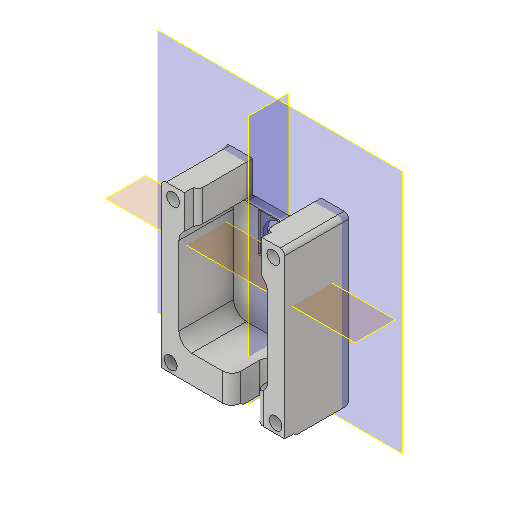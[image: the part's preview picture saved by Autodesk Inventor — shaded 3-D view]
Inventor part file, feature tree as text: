
AUTODESK INVENTOR PART (.ipt)
format: ipt  version: 2022 (Build 260153000, 153)  size: 474,624 bytes
history: native  units: mm
features: reference x19, other x12, sketch x11, extrude x10, projected_geometry x8, plane x5, fillet x2, hole x2, chamfer x1
ambient origin geometry x8: Origin, YZ Plane, XZ Plane, XY Plane, X Axis, Y Axis, Z Axis, Center Point
bodies: Solid1 (feature_tree)
feature tree (70):
  plane  "Work Plane1"
  extrude  "Extrusion1"  Depth=53.8mm
  extrude  "IM_offset"  Depth=53.8mm
  plane  "Arbeitsebene5"
  plane  "Arbeitsebene6"
  extrude  "Extrusion26"  Depth=45.0mm
  chamfer  "Fase2"  Distance=0.1mm
  plane  "Arbeitsebene9"
  extrude  "Extrusion29"  Depth=10.0mm
  extrude  "Extrusion30"  Depth=10.0mm
  plane  "Arbeitsebene10"
  extrude  "Extrusion31"  Depth=10.0mm TaperAngle=0.0deg
  fillet  "Rundung3"  Radius=7.5mm
  hole  "Bohrung2"  [1 undecoded]
  extrude  "Extrusion32"  Depth=2.0mm TaperAngle=45.0deg
  hole  "Bohrung3"  [1 undecoded]
  extrude  "Extrusion33"  Depth=10.0mm
  extrude  "Extrusion34"  Depth=10.0mm
  fillet  "Rundung4"  [1 undecoded]
  extrude  "Extrusion35"  Depth=10.0mm TaperAngle=0.0deg
  sketch  "Sketch1"  dims[d10=12.0mm d11=0.0mm d18=53.8mm]
  reference  "Reference1"
  reference  "Reference2"
  reference  "Reference3"
  reference  "Reference4"
  reference  "Reference9"
  reference  "Reference20"
  reference  "Reference21"
  reference  "Reference22"
  reference  "Reference23"
  reference  "Reference24"
  sketch  "Skizze4"  dims[d19=45.0deg d20=53.8mm]
  projected_geometry  "Projizierte Kontur1"
  sketch  "Skizze31"  dims[d21=45.0mm d22=45.0mm]
  projected_geometry  "Projizierte Kontur17"
  sketch  "Skizze34"  dims[d30=20.0mm]
  reference  "Referenz35"
  sketch  "Skizze35"  dims[d31=20.0mm]
  reference  "Referenz36"
  reference  "Referenz37"
  reference  "Referenz38"
  reference  "Referenz39"
  reference  "Referenz40"
  sketch  "Skizze37"  dims[d32=2.8mm]
  projected_geometry  "Projizierte Kontur18"
  reference  "Referenz41"
  sketch  "Skizze38"  dims[d33=2.8mm]
  reference  "Referenz42"
  sketch  "Skizze39"  dims[d34=2.8mm]
  reference  "Referenz43"
  sketch  "Skizze40"  dims[d35=3.0mm]
  projected_geometry  "Projizierte Kontur19"
  sketch  "Skizze41"  dims[d36=0.1mm]
  projected_geometry  "Projizierte Kontur20"
  sketch  "Skizze42"  dims[d37=0.1mm d38=0.1mm d39=0.1mm d40=0.2mm d41=10.0mm d42=0.0mm d181=7.5mm d182=10.0mm d183=0.0mm d184=0.5mm d185=2.0mm d186=45.0deg d193=-1.5mm d194=8.6mm d195=8.6mm d196=0.0mm d197=0.0mm d198=10.0mm d199=0.0mm d200=4.0mm d201=12.0mm d202=0.0mm d203=1.0mm d204=30.0mm d205=30.0mm d206=2.8mm d207=6.0mm d208=8.0mm d209=6.0mm d210=90.0deg d211=8.0mm d212=20.594885mm d213=0.0mm d214=0.0mm d215=2.8mm d216=6.0mm d217=4.0mm d218=2.0mm d219=90.0deg d220=8.0mm d221=20.594885mm d222=2.0mm d223=0.0mm d224=1.0mm d225=5.0mm d226=8.0mm d227=10.0mm d228=0.0mm d229=2.0mm d230=10.0mm d231=0.0mm d160=0.5mm d161=0.872665mm d162=0.5mm d163=0.872665mm]
  projected_geometry  "Projizierte Kontur21"
  projected_geometry  "Projizierte Kontur22"
  projected_geometry  "Projizierte Kontur23"
  other  "Assembly_Cube_v2_Thorlabs.iam"
  other  "10_Cube_Base:1"
  other  "00_Base_v0:1"
  other  "Assembly_Cube_Kinematic_Mirrormount_v2.iam"
  other  "Assembly_Cube_empty_1x1_v2:1"
  other  "10_Cube_1x1_v2:1"
  other  "10_Lid_1x1_v2:1"
  other  "Assembly_Cube_SEEED_Xiao_Sense_Camera_v3.iam"
  other  "00_Seeeduino Xiao:1"
  other  "00_ESP3-CAM:1"
  other  "00_ESP32_XIAO_Adapter_lid:1"
  other  "10_Cube_Lid:1"
note: 3 required parameter values undecoded (feature->parameter linkage not recoverable at this tier; creation-order binding heuristic only, values carry confidence <= 0.55)
